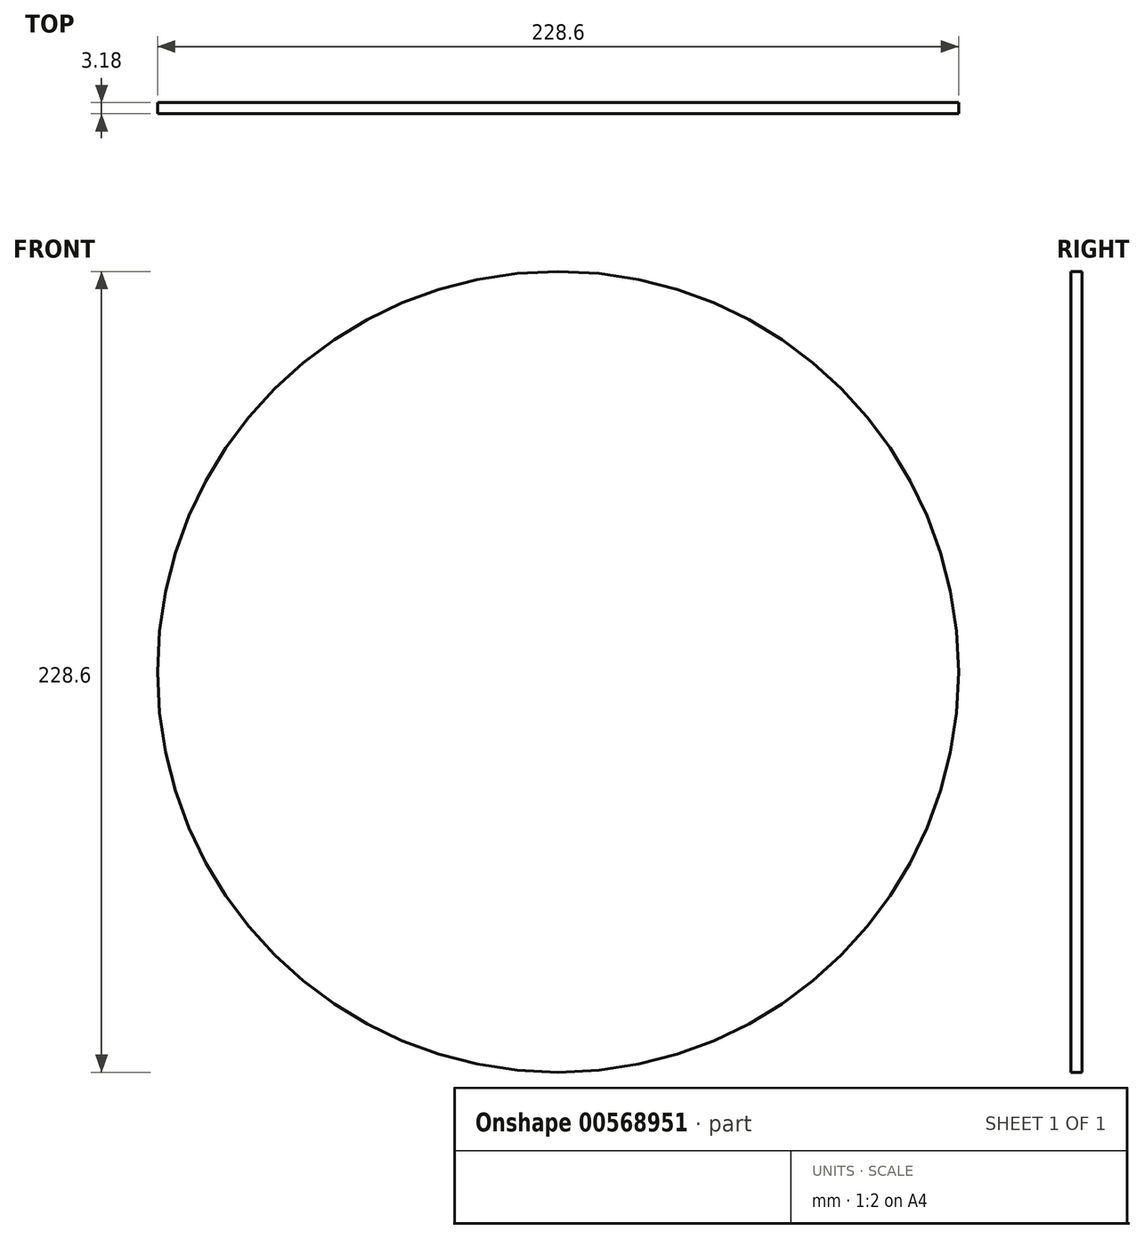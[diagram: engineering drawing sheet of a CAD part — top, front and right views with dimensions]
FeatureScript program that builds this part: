
annotation { "Feature Type Name" : "Feature", "Feature Type Description" : "" }
export const myFeature = defineFeature(function(context is Context, id is Id, definition is map)
    precondition{}
    {
        {
            var Q0;
            Q0=qCreatedBy(makeId("Front.planeOp"),FACE);
            var sketch = newSketch(context, id + "F0", { "sketchPlane" : qUnion([Q0])});
            skCircle(sketch, "E0", {"center": v(-26.05, 21.6) * mm, "radius": 114.3 * mm});
            skSolve(sketch);
        }
        {
            var Q0;
            Q0 = qSketchRegion(id + "F0", true);
            extrude(context, id + "F1", {"entities" : qUnion([Q0]), "depth" : 3.17 * mm, "offsetDistance" : 25.4 * mm});
        }
    });
